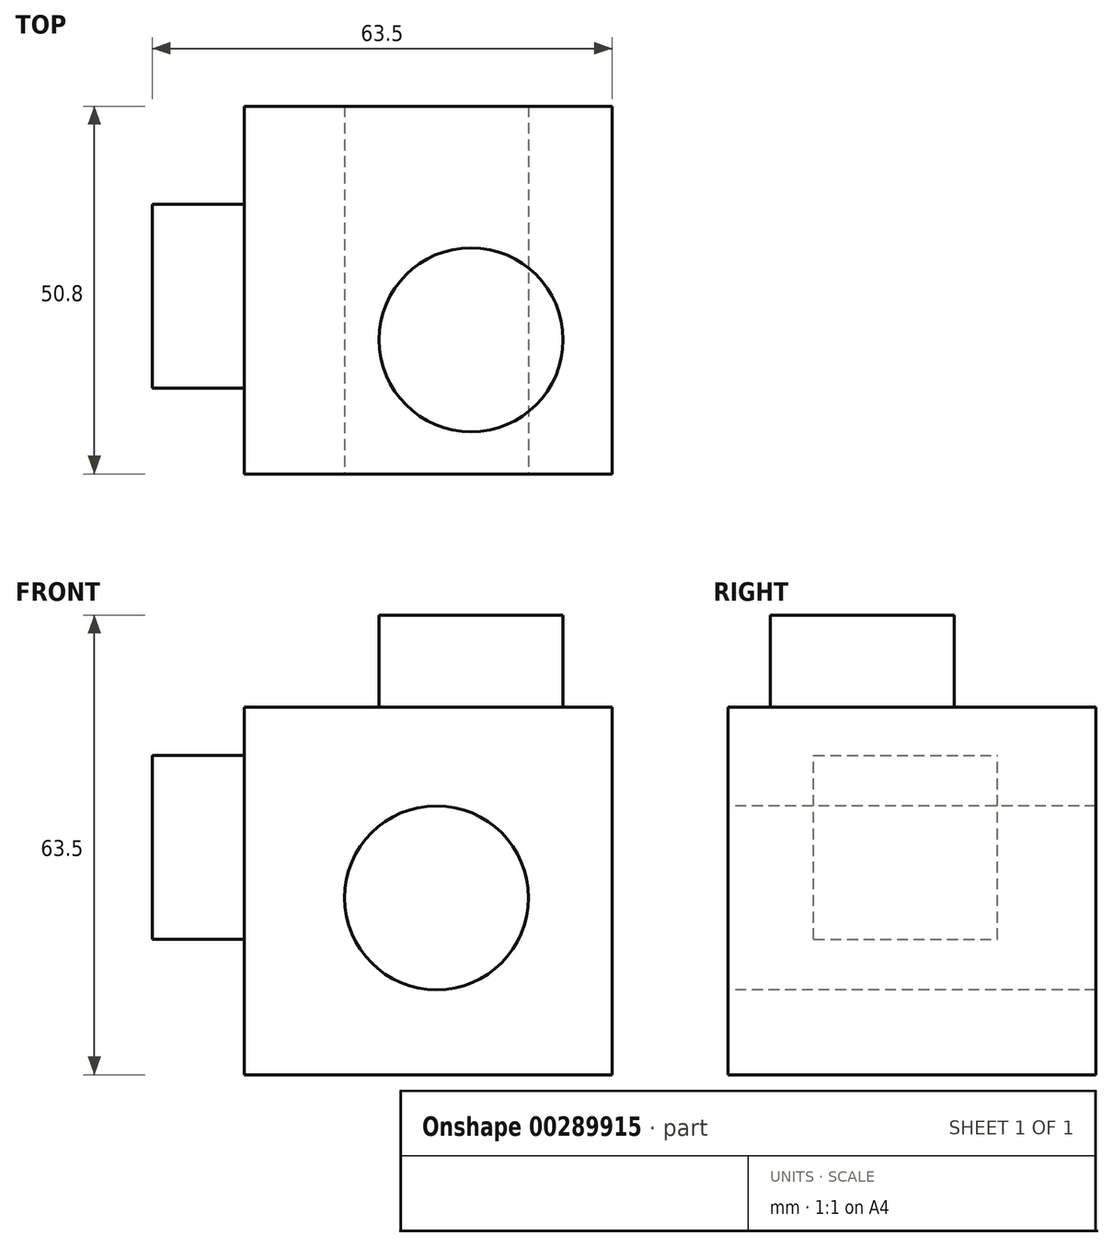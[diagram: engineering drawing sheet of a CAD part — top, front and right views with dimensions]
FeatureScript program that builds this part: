
annotation { "Feature Type Name" : "Feature", "Feature Type Description" : "" }
export const myFeature = defineFeature(function(context is Context, id is Id, definition is map)
    precondition{}
    {
        {
            var Q0;
            Q0=qCreatedBy(makeId("Front.planeOp"),FACE);
            var sketch = newSketch(context, id + "F0", { "sketchPlane" : qUnion([Q0])});
            skLineSegment(sketch, "E0.bottom", {"start": v(0, 0) * mm, "end": v(-50.8, 0) * mm});
            skLineSegment(sketch, "E0.top", {"start": v(0, 50.8) * mm, "end": v(-50.8, 50.8) * mm});
            skLineSegment(sketch, "E0.left", {"start": v(0, 0) * mm, "end": v(0, 50.8) * mm});
            skLineSegment(sketch, "E0.right", {"start": v(-50.8, 0) * mm, "end": v(-50.8, 50.8) * mm});
            skSolve(sketch);
        }
        {
            var Q0;
            Q0 = qSketchRegion(id + "F0", true);
            extrude(context, id + "F1", {"entities" : qUnion([Q0]), "depth" : 50.8 * mm});
        }
        {
            var Q0;
            Q0=makeQuery(id+"F1.opExtrude","CAP_FACE",FACE,{"disambiguationData":[OSD([sQuery(id+"F0.wireOp",EDGE,"E0.bottom"),sQuery(id+"F0.wireOp",EDGE,"E0.top"),sQuery(id+"F0.wireOp",EDGE,"E0.left"),sQuery(id+"F0.wireOp",EDGE,"E0.right")])],"isStart":false});
            var sketch = newSketch(context, id + "F2", { "sketchPlane" : qUnion([Q0])});
            skCircle(sketch, "E1", {"center": v(-24.25, 24.44) * mm, "radius": 12.7 * mm});
            skSolve(sketch);
        }
        {
            var Q0;
            Q0 = qSketchRegion(id + "F2", true);
            extrude(context, id + "F3", {"entities" : qUnion([Q0]), "operationType" : NewBodyOperationType.REMOVE, "oppositeDirection" : true, "depth" : 50.8 * mm});
        }
        {
            var Q0;
            Q0=makeQuery(id+"F1.opExtrude","SWEPT_FACE",FACE,{"disambiguationData":[OSD([sQuery(id+"F0.wireOp",EDGE,"E0.top")])]});
            var sketch = newSketch(context, id + "F4", { "sketchPlane" : qUnion([Q0])});
            skCircle(sketch, "E2", {"center": v(-19.48, -32.27) * mm, "radius": 12.7 * mm});
            skSolve(sketch);
        }
        {
            var Q0;
            Q0 = qSketchRegion(id + "F4", true);
            extrude(context, id + "F5", {"entities" : qUnion([Q0]), "operationType" : NewBodyOperationType.ADD, "depth" : 12.7 * mm});
        }
        {
            var Q0;
            Q0=makeQuery(id+"F1.opExtrude","SWEPT_FACE",FACE,{"disambiguationData":[OSD([sQuery(id+"F0.wireOp",EDGE,"E0.right")])]});
            var sketch = newSketch(context, id + "F6", { "sketchPlane" : qUnion([Q0])});
            skLineSegment(sketch, "E3.bottom", {"start": v(38.96, 18.71) * mm, "end": v(13.56, 18.71) * mm});
            skLineSegment(sketch, "E3.top", {"start": v(38.96, 44.11) * mm, "end": v(13.56, 44.11) * mm});
            skLineSegment(sketch, "E3.left", {"start": v(38.96, 18.71) * mm, "end": v(38.96, 44.11) * mm});
            skLineSegment(sketch, "E3.right", {"start": v(13.56, 18.71) * mm, "end": v(13.56, 44.11) * mm});
            skSolve(sketch);
        }
        {
            var Q0;
            Q0 = qSketchRegion(id + "F6", true);
            extrude(context, id + "F7", {"entities" : qUnion([Q0]), "operationType" : NewBodyOperationType.ADD, "depth" : 12.7 * mm});
        }
    });
